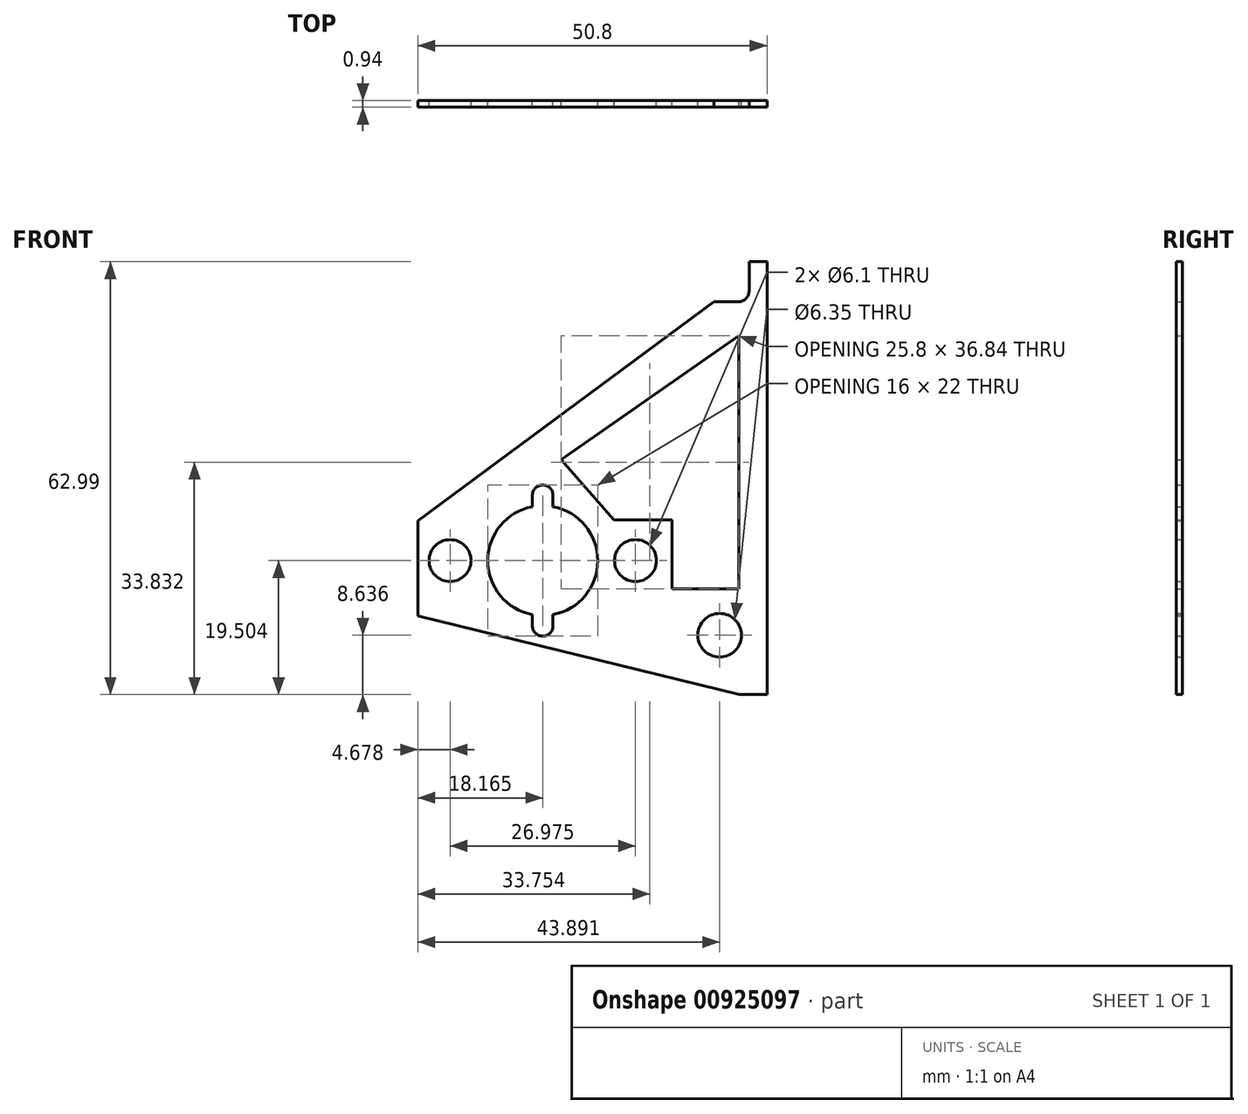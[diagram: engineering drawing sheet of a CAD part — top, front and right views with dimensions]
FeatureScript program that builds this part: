
annotation { "Feature Type Name" : "Feature", "Feature Type Description" : "" }
export const myFeature = defineFeature(function(context is Context, id is Id, definition is map)
    precondition{}
    {
        {
            assignVariable(context, id + "F0", {"name" : "thickness", "anyValue" : .93});
        }
        {
            var Q0;
            Q0=qCreatedBy(makeId("Front.planeOp"),FACE);
            var sketch = newSketch(context, id + "F1", { "sketchPlane" : qUnion([Q0])});
            skLineSegment(sketch, "E0.bottom", {"start": v(0, 0) * mm, "end": v(-50.8, 0) * mm});
            skLineSegment(sketch, "E0.top", {"start": v(0, 63) * mm, "end": v(-2.62, 63) * mm});
            skLineSegment(sketch, "E0.left", {"start": v(0, 0) * mm, "end": v(0, 63) * mm});
            skLineSegment(sketch, "E1.top", {"start": v(-4.2, 57.15) * mm, "end": v(-50.8, 57.15) * mm});
            skLineSegment(sketch, "E1.right", {"start": v(-50.8, 0) * mm, "end": v(-50.8, 57.15) * mm});
            skLineSegment(sketch, "E2", {"start": v(-2.62, 63) * mm, "end": v(-2.62, 58.74) * mm});
            skArc(sketch, "E3.filletArc", {"start": v(-4.2, 57.15) * mm, "mid": v(-3.08, 57.61) * mm, "end": v(-2.62, 58.74) * mm});
            skCircle(sketch, "E4", {"center": v(-6.9, 8.64) * mm, "radius": 3.18 * mm});
            skCircle(sketch, "E5", {"center": v(-32.63, 19.5) * mm, "radius": 8 * mm});
            skCircle(sketch, "E6", {"center": v(-46.12, 19.5) * mm, "radius": 3.05 * mm});
            skCircle(sketch, "E7", {"center": v(-19.15, 19.5) * mm, "radius": 3.05 * mm});
            skLineSegment(sketch, "E8", {"start": v(-46.12, 19.5) * mm, "end": v(-32.63, 19.5) * mm, "construction": true});
            skLineSegment(sketch, "E9", {"start": v(-19.15, 19.5) * mm, "end": v(-32.63, 19.5) * mm, "construction": true});
            skCircle(sketch, "E10", {"center": v(-32.63, 29) * mm, "radius": 1.5 * mm});
            skCircle(sketch, "E11", {"center": v(-32.63, 10) * mm, "radius": 1.5 * mm});
            skLineSegment(sketch, "E12", {"start": v(-32.63, 29) * mm, "end": v(-32.63, 10) * mm, "construction": true});
            skLineSegment(sketch, "E13", {"start": v(-31.14, 29) * mm, "end": v(-31.14, 27.36) * mm});
            skLineSegment(sketch, "E14", {"start": v(-34.13, 29) * mm, "end": v(-34.13, 27.36) * mm});
            skLineSegment(sketch, "E15", {"start": v(-34.13, 10) * mm, "end": v(-34.13, 11.64) * mm});
            skLineSegment(sketch, "E16", {"start": v(-31.14, 10) * mm, "end": v(-31.14, 11.64) * mm});
            skLineSegment(sketch, "E17", {"start": v(-50.8, 25.33) * mm, "end": v(-7.75, 57.15) * mm});
            skLineSegment(sketch, "E18", {"start": v(-4.15, 52.25) * mm, "end": v(-4.15, 15.4) * mm});
            skLineSegment(sketch, "E19", {"start": v(-4.15, 15.4) * mm, "end": v(-13.82, 15.4) * mm});
            skLineSegment(sketch, "E20", {"start": v(-13.82, 15.4) * mm, "end": v(-13.82, 25.45) * mm});
            skLineSegment(sketch, "E21", {"start": v(-13.82, 25.45) * mm, "end": v(-22.27, 25.45) * mm});
            skLineSegment(sketch, "E22", {"start": v(-22.27, 25.45) * mm, "end": v(-29.94, 34.19) * mm});
            skLineSegment(sketch, "E23", {"start": v(-29.94, 34.19) * mm, "end": v(-4.15, 52.25) * mm});
            skLineSegment(sketch, "E24", {"start": v(-50.8, 11.43) * mm, "end": v(-4.07, 0) * mm});
            skSolve(sketch);
        }
        {
            var Q0;
            Q0=makeQuery(id+"F1.imprint","IMPRINT",FACE,{"disambiguationData":[TD([[makeQuery(id+"F1.imprint","IMPRINT",EDGE,{"derivedFrom":sQuery(id+"F1.wireOp",EDGE,"E0.top")}),1.0]])]});
            extrude(context, id + "F2", {"entities" : qUnion([Q0]), "depth" : (getVariable(context, 'thickness')) * mm, "offsetDistance" : 25.4 * mm, "symmetric" : true});
        }
    });
